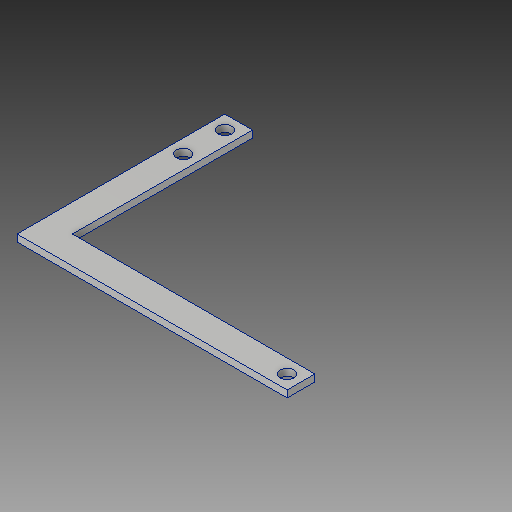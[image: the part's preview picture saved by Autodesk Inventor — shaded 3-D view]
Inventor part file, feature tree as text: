
AUTODESK INVENTOR PART (.ipt)
format: ipt  version: 2018.1 (Build 221171000, 171)  size: 114,176 bytes
history: native  units: mm
features: extrude x1, sketch x1
ambient origin geometry x8: Origin, YZ Plane, XZ Plane, XY Plane, X Axis, Y Axis, Z Axis, Center Point
bodies: Body1 (feature_tree)
feature tree (2):
  extrude  "押し出し4"  Depth=195.0mm
  sketch  "スケッチ1"
